# Revit family: Toilet_Paper_Holder-American_Standard-Estate-7722230_Series
name_source: partatom
category: Specialty Equipment
units: mm (PartAtom-declared; Revit-internal decimal feet)

## family parameters
Cut with Voids When Loaded = No
Host = Face
OmniClass Number = 23.40.20.21.21
OmniClass Title = Toilet Paper Dispensers
Part Type = Normal
Room Calculation Point = No
Round Connector Dimension = Use Diameter
Shared = Yes

## types (5) — shared parameters
Assembly Code = C1030220
Default Elevation = 44"
Description = Estate Toilet Paper Holder
Height = 2 1/4"
Installation Type = Wall Mounted
Length = 3 7/8"
Manufacturer = American Standard
Product Documentation Link = https://lixil.cdn.celum.cloud
Product Page URL = https://www.americanstandard-us.com
Revised Date = 02/28/2024
URL = http://www.americanstandard-us.com
Warranty Information = Limited Lifetime Warranty
Width = 8 3/4"

## per-type parameters (varying)
| type | Finish | Material |
| 7722230.002 | Metal-American Standard-002-Polished Chrome | Metal-American Standard-002-Polished Chrome |
| 7722230.295 | Metal-American Standard-295-Brushed Nickel | Metal-American Standard-295-Brushed Nickel |
| 7722230.013 | Metal-American Standard-013-Polished Nickel | Metal-American Standard-013-Polished Nickel |
| 7722230.278 | Metal-American Standard-278-Legacy Bronze | Metal-American Standard-278-Legacy Bronze |
| 7722230.243 | Metal-American Standard-295-Brushed Nickel | Metal-American Standard-295-Brushed Nickel |

note: column(s) folded — value = type name in every type: Model

## geometry (parser evidence)
native form markers: Sweep x3
no freeform markers — native parametric forms only
